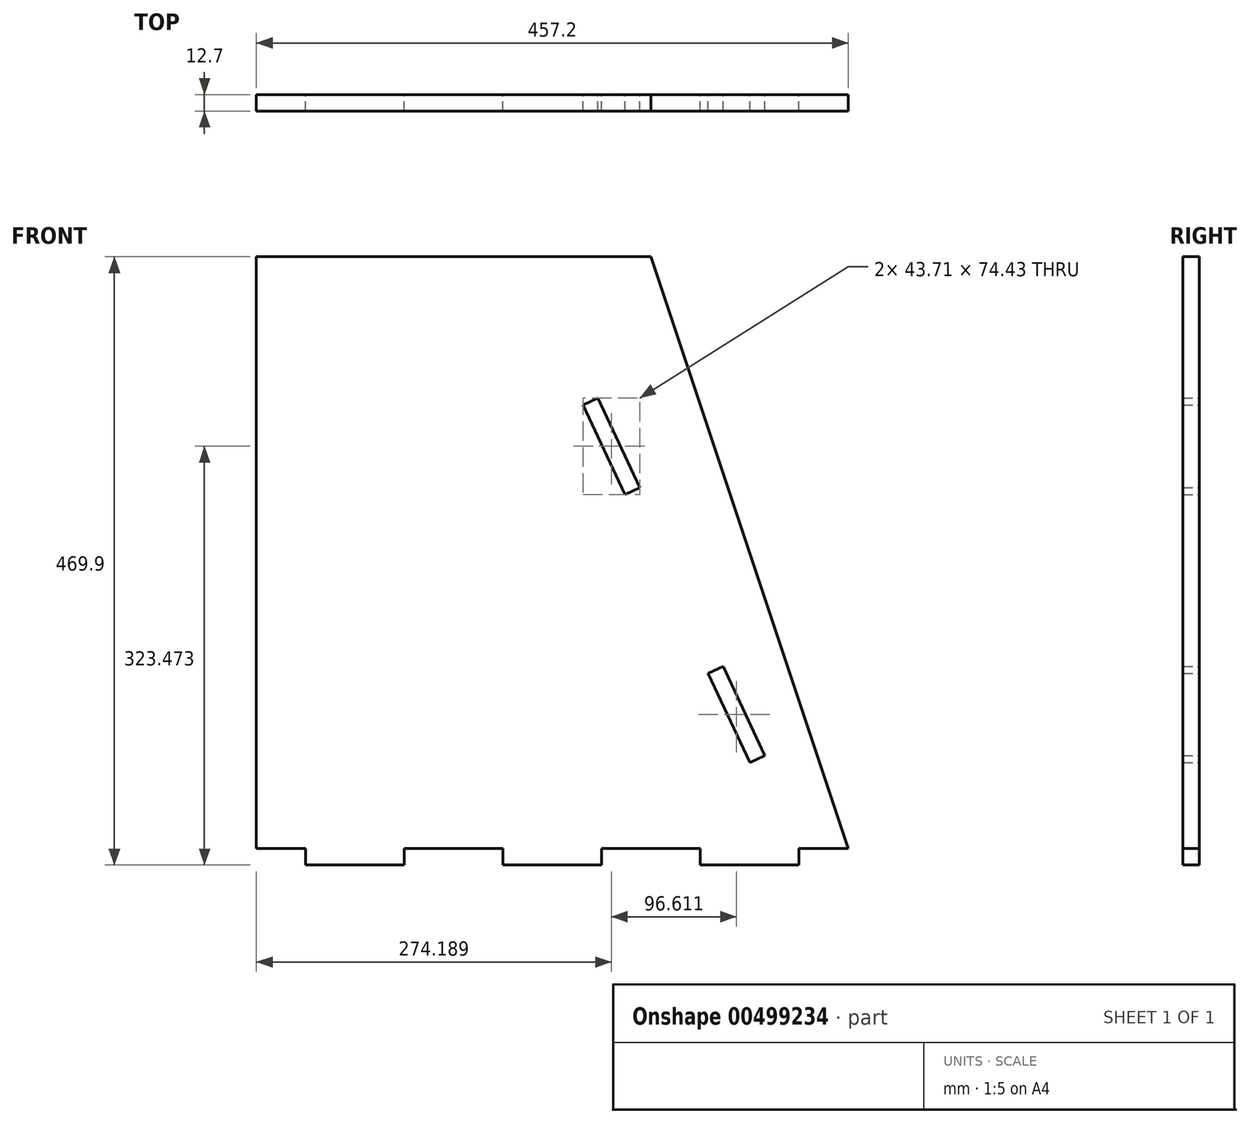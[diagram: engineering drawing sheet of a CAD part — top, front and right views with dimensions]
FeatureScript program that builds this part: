
annotation { "Feature Type Name" : "Feature", "Feature Type Description" : "" }
export const myFeature = defineFeature(function(context is Context, id is Id, definition is map)
    precondition{}
    {
        {
            var Q0;
            Q0=qCreatedBy(makeId("Front.planeOp"),FACE);
            var sketch = newSketch(context, id + "F0", { "sketchPlane" : qUnion([Q0])});
            skLineSegment(sketch, "E0", {"start": v(-318.55, 32.03) * mm, "end": v(-318.55, -425.17) * mm});
            skLineSegment(sketch, "E1", {"start": v(-318.55, -425.17) * mm, "end": v(-280.45, -425.17) * mm});
            skLineSegment(sketch, "E2", {"start": v(138.65, -425.17) * mm, "end": v(-13.75, 32.03) * mm});
            skLineSegment(sketch, "E3", {"start": v(-13.75, 32.03) * mm, "end": v(-318.55, 32.03) * mm});
            skLineSegment(sketch, "E4", {"start": v(-318.55, -425.17) * mm, "end": v(-280.45, -425.17) * mm, "construction": true});
            skLineSegment(sketch, "E5", {"start": v(-280.45, -425.17) * mm, "end": v(-318.55, -425.17) * mm, "construction": true});
            skLineSegment(sketch, "E6.top", {"start": v(-280.45, -437.87) * mm, "end": v(-204.25, -437.87) * mm});
            skLineSegment(sketch, "E6.left", {"start": v(-280.45, -425.17) * mm, "end": v(-280.45, -437.87) * mm});
            skLineSegment(sketch, "E6.right", {"start": v(-204.25, -425.17) * mm, "end": v(-204.25, -437.87) * mm});
            skLineSegment(sketch, "E7.trimOffspring", {"start": v(-204.25, -425.17) * mm, "end": v(-128.05, -425.17) * mm});
            skLineSegment(sketch, "E8", {"start": v(-204.25, -425.17) * mm, "end": v(-128.05, -425.17) * mm, "construction": true});
            skLineSegment(sketch, "E9", {"start": v(-128.05, -425.17) * mm, "end": v(-204.25, -425.17) * mm, "construction": true});
            skLineSegment(sketch, "E10.top", {"start": v(-128.05, -437.87) * mm, "end": v(-51.85, -437.87) * mm});
            skLineSegment(sketch, "E10.left", {"start": v(-128.05, -425.17) * mm, "end": v(-128.05, -437.87) * mm});
            skLineSegment(sketch, "E10.right", {"start": v(-51.85, -425.17) * mm, "end": v(-51.85, -437.87) * mm});
            skLineSegment(sketch, "E11.trimOffspring", {"start": v(-51.85, -425.17) * mm, "end": v(24.35, -425.17) * mm});
            skLineSegment(sketch, "E12", {"start": v(-51.85, -425.17) * mm, "end": v(24.35, -425.17) * mm, "construction": true});
            skLineSegment(sketch, "E13", {"start": v(24.35, -425.17) * mm, "end": v(-51.85, -425.17) * mm, "construction": true});
            skLineSegment(sketch, "E14.top", {"start": v(24.35, -437.87) * mm, "end": v(100.55, -437.87) * mm});
            skLineSegment(sketch, "E14.left", {"start": v(24.35, -425.17) * mm, "end": v(24.35, -437.87) * mm});
            skLineSegment(sketch, "E14.right", {"start": v(100.55, -425.17) * mm, "end": v(100.55, -437.87) * mm});
            skLineSegment(sketch, "E15.trimOffspring", {"start": v(100.55, -425.17) * mm, "end": v(138.65, -425.17) * mm});
            skLineSegment(sketch, "E16", {"start": v(100.55, -425.17) * mm, "end": v(24.35, -425.17) * mm, "construction": true});
            skPoint(sketch, "E17", {"position": v(-92.67, -10.8) * mm});
            skLineSegment(sketch, "E18", {"start": v(100.55, -425.17) * mm, "end": v(-92.67, -10.8) * mm, "construction": true});
            skLineSegment(sketch, "E19", {"start": v(-92.67, -10.8) * mm, "end": v(-98.42, -13.49) * mm, "construction": true});
            skLineSegment(sketch, "E20", {"start": v(-98.42, -13.49) * mm, "end": v(-50.12, -117.08) * mm, "construction": true});
            skLineSegment(sketch, "E21", {"start": v(-38.6, -111.71) * mm, "end": v(-22.5, -146.24) * mm});
            skLineSegment(sketch, "E22", {"start": v(-22.5, -146.24) * mm, "end": v(-34.01, -151.61) * mm});
            skLineSegment(sketch, "E23", {"start": v(-34.01, -151.61) * mm, "end": v(-50.12, -117.08) * mm});
            skLineSegment(sketch, "E24.MirrorCS", {"start": v(-66.22, -82.55) * mm, "end": v(-50.12, -117.08) * mm});
            skLineSegment(sketch, "E25.MirrorCS", {"start": v(-38.6, -111.71) * mm, "end": v(-54.7, -77.18) * mm});
            skLineSegment(sketch, "E26.MirrorCS", {"start": v(-54.7, -77.18) * mm, "end": v(-66.22, -82.55) * mm});
            skLineSegment(sketch, "E27", {"start": v(3.94, -217.99) * mm, "end": v(-6.67, -222.94) * mm, "construction": true});
            skLineSegment(sketch, "E28.MirrorCS", {"start": v(30.4, -289.73) * mm, "end": v(46.5, -324.26) * mm});
            skLineSegment(sketch, "E29.MirrorCS", {"start": v(58, -318.9) * mm, "end": v(41.9, -284.37) * mm});
            skLineSegment(sketch, "E30.MirrorCS", {"start": v(58, -318.9) * mm, "end": v(74.1, -353.43) * mm});
            skLineSegment(sketch, "E31.MirrorCS", {"start": v(74.1, -353.43) * mm, "end": v(62.6, -358.8) * mm});
            skLineSegment(sketch, "E32.MirrorCS", {"start": v(41.9, -284.37) * mm, "end": v(30.4, -289.73) * mm});
            skLineSegment(sketch, "E33", {"start": v(46.5, -324.26) * mm, "end": v(62.6, -358.8) * mm});
            skSolve(sketch);
        }
        {
            var Q0;
            Q0 = qSketchRegion(id + "F0", true);
            extrude(context, id + "F1", {"entities" : qUnion([Q0]), "depth" : 12.7 * mm, "offsetDistance" : 25.4 * mm});
        }
    });
